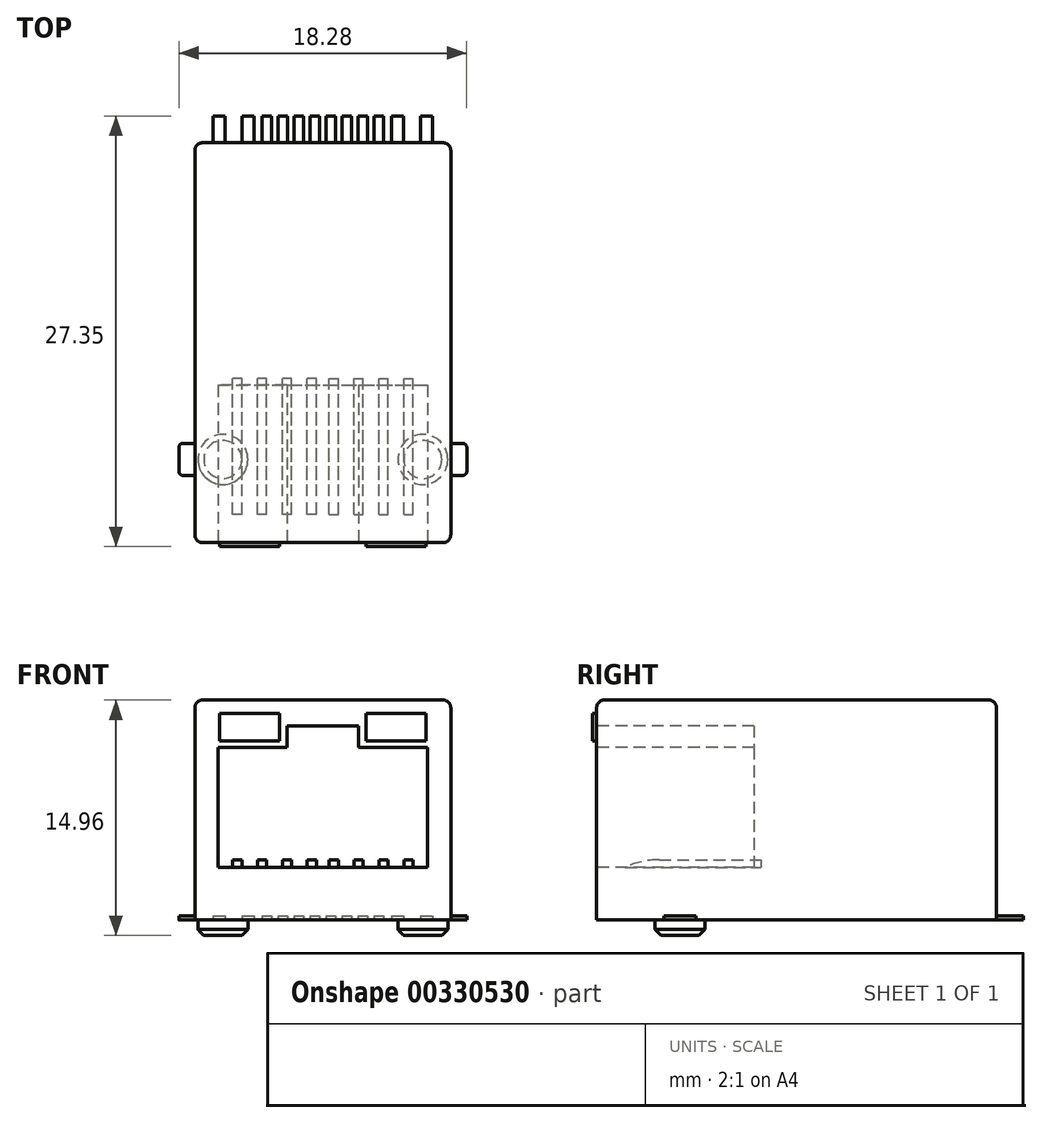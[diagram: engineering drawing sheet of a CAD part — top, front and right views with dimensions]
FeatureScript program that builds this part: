
annotation { "Feature Type Name" : "Feature", "Feature Type Description" : "" }
export const myFeature = defineFeature(function(context is Context, id is Id, definition is map)
    precondition{}
    {
        {
            var Q0;
            Q0=qCreatedBy(makeId("Top.planeOp"),FACE);
            var sketch = newSketch(context, id + "F0", { "sketchPlane" : qUnion([Q0])});
            skLineSegment(sketch, "E0.bottom", {"start": v(8.13, -12.7) * mm, "end": v(-8.13, -12.7) * mm});
            skLineSegment(sketch, "E0.top", {"start": v(8.13, 12.7) * mm, "end": v(-8.13, 12.7) * mm});
            skLineSegment(sketch, "E0.left", {"start": v(8.13, -12.7) * mm, "end": v(8.13, 12.7) * mm});
            skLineSegment(sketch, "E0.right", {"start": v(-8.13, -12.7) * mm, "end": v(-8.13, 12.7) * mm});
            skPoint(sketch, "E0.middle", {"position": v(0, 0) * mm});
            skSolve(sketch);
        }
        {
            var Q0;
            Q0=qSketchRegion(id+"F0",true);
            extrude(context, id + "F1", {"entities" : qUnion([Q0]), "depth" : 13.97 * mm, "offsetDistance" : 25 * mm});
        }
        {
            var Q0;
            Q0=makeQuery(id+"FJxkkNZS4rezTmz_1.boolean.opBoolean","MERGE",EDGE,{"derivedFrom":[makeQuery(id+"F1.opExtrude","SWEPT_EDGE",EDGE,{"disambiguationData":[OSD([sQuery(id+"F0.wireOp",EDGE,"E0.bottom"),sQuery(id+"F0.wireOp",EDGE,"E0.right")])]}),makeQuery(id+"FJxkkNZS4rezTmz_1.opExtrude","SWEPT_EDGE",EDGE,{"disambiguationData":[OSD([sQuery(id+"F9NPPUefej9rEKj_1.wireOp",EDGE,"desPq1yY-o5Qy-SBm8-Lvxq-VWqHqrpmvovc.bottom"),sQuery(id+"F9NPPUefej9rEKj_1.wireOp",EDGE,"desPq1yY-o5Qy-SBm8-Lvxq-VWqHqrpmvovc.right")])]})]});
            var Q1;
            Q1=makeQuery(id+"FJxkkNZS4rezTmz_1.boolean.opBoolean","MERGE",EDGE,{"derivedFrom":[makeQuery(id+"F1.opExtrude","SWEPT_EDGE",EDGE,{"disambiguationData":[OSD([sQuery(id+"F0.wireOp",EDGE,"E0.bottom"),sQuery(id+"F0.wireOp",EDGE,"E0.left")])]}),makeQuery(id+"FJxkkNZS4rezTmz_1.opExtrude","SWEPT_EDGE",EDGE,{"disambiguationData":[OSD([sQuery(id+"F9NPPUefej9rEKj_1.wireOp",EDGE,"desPq1yY-o5Qy-SBm8-Lvxq-VWqHqrpmvovc.bottom"),sQuery(id+"F9NPPUefej9rEKj_1.wireOp",EDGE,"desPq1yY-o5Qy-SBm8-Lvxq-VWqHqrpmvovc.left")])]})]});
            var Q2;
            Q2=makeQuery(id+"F1.opExtrude","SWEPT_EDGE",EDGE,{"disambiguationData":[OSD([sQuery(id+"F0.wireOp",EDGE,"E0.top"),sQuery(id+"F0.wireOp",EDGE,"E0.left")])]});
            var Q3;
            Q3=makeQuery(id+"F1.opExtrude","SWEPT_EDGE",EDGE,{"disambiguationData":[OSD([sQuery(id+"F0.wireOp",EDGE,"E0.top"),sQuery(id+"F0.wireOp",EDGE,"E0.right")])]});
            var Q4;
            Q4=makeQuery(id+"F1.opExtrude","CAP_EDGE",EDGE,{"disambiguationData":[OSD([sQuery(id+"F0.wireOp",EDGE,"E0.bottom")])],"isStart":false});
            var Q5;
            Q5=makeQuery(id+"F1.opExtrude","CAP_EDGE",EDGE,{"disambiguationData":[OSD([sQuery(id+"F0.wireOp",EDGE,"E0.right")])],"isStart":false});
            var Q6;
            Q6=makeQuery(id+"F1.opExtrude","CAP_EDGE",EDGE,{"disambiguationData":[OSD([sQuery(id+"F0.wireOp",EDGE,"E0.top")])],"isStart":false});
            var Q7;
            Q7=makeQuery(id+"F1.opExtrude","CAP_EDGE",EDGE,{"disambiguationData":[OSD([sQuery(id+"F0.wireOp",EDGE,"E0.left")])],"isStart":false});
            var Q8;
            Q8=makeQuery(id+"FJxkkNZS4rezTmz_1.opExtrude","CAP_EDGE",EDGE,{"disambiguationData":[OSD([sQuery(id+"F9NPPUefej9rEKj_1.wireOp",EDGE,"desPq1yY-o5Qy-SBm8-Lvxq-VWqHqrpmvovc.bottom")])],"isStart":false});
            var Q9;
            Q9=makeQuery(id+"FJxkkNZS4rezTmz_1.opExtrude","CAP_EDGE",EDGE,{"disambiguationData":[OSD([sQuery(id+"F9NPPUefej9rEKj_1.wireOp",EDGE,"desPq1yY-o5Qy-SBm8-Lvxq-VWqHqrpmvovc.right")])],"isStart":false});
            var Q10;
            Q10=makeQuery(id+"FJxkkNZS4rezTmz_1.opExtrude","CAP_EDGE",EDGE,{"disambiguationData":[OSD([sQuery(id+"F9NPPUefej9rEKj_1.wireOp",EDGE,"desPq1yY-o5Qy-SBm8-Lvxq-VWqHqrpmvovc.left")])],"isStart":false});
            fillet(context, id + "F2", {"entities" : qUnion([Q0, Q1, Q2, Q3, Q4, Q5, Q6, Q7, Q8, Q9, Q10]), "radius" : .5 * mm, "tangentPropagation" : true, "allowEdgeOverflow" : false});
        }
        {
            var Q0;
            Q0=makeQuery(id+"FJxkkNZS4rezTmz_1.boolean.opBoolean","MERGE",FACE,{"derivedFrom":[makeQuery(id+"F1.opExtrude","SWEPT_FACE",FACE,{"disambiguationData":[OSD([sQuery(id+"F0.wireOp",EDGE,"E0.bottom")])]}),makeQuery(id+"FJxkkNZS4rezTmz_1.opExtrude","SWEPT_FACE",FACE,{"disambiguationData":[OSD([sQuery(id+"F9NPPUefej9rEKj_1.wireOp",EDGE,"desPq1yY-o5Qy-SBm8-Lvxq-VWqHqrpmvovc.bottom")])]})]});
            var sketch = newSketch(context, id + "F3", { "sketchPlane" : qUnion([Q0])});
            skLineSegment(sketch, "E1", {"start": v(0, 13.47) * mm, "end": v(0, 0) * mm, "construction": true});
            skLineSegment(sketch, "E2", {"start": v(0, 12.33) * mm, "end": v(2.28, 12.33) * mm});
            skLineSegment(sketch, "E3", {"start": v(2.28, 12.33) * mm, "end": v(2.28, 10.96) * mm});
            skLineSegment(sketch, "E4", {"start": v(2.28, 10.96) * mm, "end": v(6.66, 10.96) * mm});
            skLineSegment(sketch, "E5", {"start": v(6.66, 10.96) * mm, "end": v(6.66, 3.33) * mm});
            skLineSegment(sketch, "E6", {"start": v(6.66, 3.33) * mm, "end": v(0, 3.33) * mm});
            skLineSegment(sketch, "E7.MirrorCS", {"start": v(-6.66, 3.33) * mm, "end": v(0, 3.33) * mm});
            skLineSegment(sketch, "E8.MirrorCS", {"start": v(-6.66, 10.96) * mm, "end": v(-6.66, 3.33) * mm});
            skLineSegment(sketch, "E9.MirrorCS", {"start": v(-2.28, 10.96) * mm, "end": v(-6.66, 10.96) * mm});
            skLineSegment(sketch, "E10.MirrorCS", {"start": v(0, 12.33) * mm, "end": v(-2.28, 12.33) * mm});
            skLineSegment(sketch, "E11.MirrorCS", {"start": v(-2.28, 12.33) * mm, "end": v(-2.28, 10.96) * mm});
            skSolve(sketch);
        }
        {
            var Q0;
            Q0=qSketchRegion(id+"F3",true);
            extrude(context, id + "F4", {"entities" : qUnion([Q0]), "operationType" : NewBodyOperationType.REMOVE, "oppositeDirection" : true, "depth" : 10 * mm, "offsetDistance" : 25 * mm});
        }
        {
            var Q0;
            Q0=makeQuery(id+"F4.boolean.opBoolean","COPY",FACE,{"derivedFrom":makeQuery(id+"F4.opExtrude","SWEPT_FACE",FACE,{"disambiguationData":[OSD([sQuery(id+"F3.wireOp",EDGE,"E6"),sQuery(id+"F3.wireOp",EDGE,"E7.MirrorCS")])]})});
            var sketch = newSketch(context, id + "F5", { "sketchPlane" : qUnion([Q0])});
            skLineSegment(sketch, "E12", {"start": v(0, -12.7) * mm, "end": v(0, -2.7) * mm, "construction": true});
            skLineSegment(sketch, "E13.bottom", {"start": v(0.4, -10.9) * mm, "end": v(0.99, -10.9) * mm});
            skLineSegment(sketch, "E13.top", {"start": v(0.4, -2.26) * mm, "end": v(0.99, -2.26) * mm});
            skLineSegment(sketch, "E13.left", {"start": v(0.4, -10.9) * mm, "end": v(0.4, -2.26) * mm});
            skLineSegment(sketch, "E13.right", {"start": v(0.99, -10.9) * mm, "end": v(0.99, -2.26) * mm});
            skLineSegment(sketch, "E14.1.0.0", {"start": v(1.98, -10.9) * mm, "end": v(2.57, -10.9) * mm});
            skLineSegment(sketch, "E14.1.0.1", {"start": v(1.98, -2.26) * mm, "end": v(2.57, -2.26) * mm});
            skLineSegment(sketch, "E14.1.0.2", {"start": v(1.98, -10.9) * mm, "end": v(1.98, -2.26) * mm});
            skLineSegment(sketch, "E14.1.0.3", {"start": v(2.57, -10.9) * mm, "end": v(2.57, -2.26) * mm});
            skLineSegment(sketch, "E14.2.0.0", {"start": v(3.56, -10.9) * mm, "end": v(4.15, -10.9) * mm});
            skLineSegment(sketch, "E14.2.0.1", {"start": v(3.56, -2.26) * mm, "end": v(4.15, -2.26) * mm});
            skLineSegment(sketch, "E14.2.0.2", {"start": v(3.56, -10.9) * mm, "end": v(3.56, -2.26) * mm});
            skLineSegment(sketch, "E14.2.0.3", {"start": v(4.15, -10.9) * mm, "end": v(4.15, -2.26) * mm});
            skLineSegment(sketch, "E14.3.0.0", {"start": v(5.14, -10.9) * mm, "end": v(5.73, -10.9) * mm});
            skLineSegment(sketch, "E14.3.0.1", {"start": v(5.14, -2.26) * mm, "end": v(5.73, -2.26) * mm});
            skLineSegment(sketch, "E14.3.0.2", {"start": v(5.14, -10.9) * mm, "end": v(5.14, -2.26) * mm});
            skLineSegment(sketch, "E14.3.0.3", {"start": v(5.73, -10.9) * mm, "end": v(5.73, -2.26) * mm});
            skLineSegment(sketch, "E14.direction1", {"start": v(0.4, -10.9) * mm, "end": v(1.98, -10.9) * mm, "construction": true});
            skLineSegment(sketch, "E15.MirrorCS", {"start": v(-0.4, -10.9) * mm, "end": v(-0.99, -10.9) * mm});
            skLineSegment(sketch, "E16.MirrorCS", {"start": v(-4.15, -10.9) * mm, "end": v(-4.15, -2.26) * mm});
            skLineSegment(sketch, "E17.MirrorCS", {"start": v(-3.56, -10.9) * mm, "end": v(-3.56, -2.26) * mm});
            skLineSegment(sketch, "E18.MirrorCS", {"start": v(-3.56, -2.26) * mm, "end": v(-4.15, -2.26) * mm});
            skLineSegment(sketch, "E19.MirrorCS", {"start": v(-3.56, -10.9) * mm, "end": v(-4.15, -10.9) * mm});
            skLineSegment(sketch, "E20.MirrorCS", {"start": v(-2.57, -10.9) * mm, "end": v(-2.57, -2.26) * mm});
            skLineSegment(sketch, "E21.MirrorCS", {"start": v(-1.98, -10.9) * mm, "end": v(-1.98, -2.26) * mm});
            skLineSegment(sketch, "E22.MirrorCS", {"start": v(-1.98, -2.26) * mm, "end": v(-2.57, -2.26) * mm});
            skLineSegment(sketch, "E23.MirrorCS", {"start": v(-1.98, -10.9) * mm, "end": v(-2.57, -10.9) * mm});
            skLineSegment(sketch, "E24.MirrorCS", {"start": v(-0.99, -10.9) * mm, "end": v(-0.99, -2.26) * mm});
            skLineSegment(sketch, "E25.MirrorCS", {"start": v(-0.4, -10.9) * mm, "end": v(-0.4, -2.26) * mm});
            skLineSegment(sketch, "E26.MirrorCS", {"start": v(-0.4, -2.26) * mm, "end": v(-0.99, -2.26) * mm});
            skLineSegment(sketch, "E27.MirrorCS", {"start": v(-5.73, -10.9) * mm, "end": v(-5.73, -2.26) * mm});
            skLineSegment(sketch, "E28.MirrorCS", {"start": v(-5.14, -10.9) * mm, "end": v(-5.14, -2.26) * mm});
            skLineSegment(sketch, "E29.MirrorCS", {"start": v(-5.14, -2.26) * mm, "end": v(-5.73, -2.26) * mm});
            skLineSegment(sketch, "E30.MirrorCS", {"start": v(-0.4, -10.9) * mm, "end": v(-1.98, -10.9) * mm, "construction": true});
            skLineSegment(sketch, "E31.MirrorCS", {"start": v(-5.14, -10.9) * mm, "end": v(-5.73, -10.9) * mm});
            skSolve(sketch);
        }
        {
            var Q0;
            Q0=qSketchRegion(id+"F5",true);
            extrude(context, id + "F6", {"entities" : qUnion([Q0]), "depth" : .5 * mm, "offsetDistance" : 25 * mm});
        }
        {
            var Q0;
            Q0=makeQuery(id+"F6.opExtrude","CAP_EDGE",EDGE,{"disambiguationData":[OSD([sQuery(id+"F5.wireOp",EDGE,"E31.MirrorCS")])],"isStart":false});
            var Q1;
            Q1=makeQuery(id+"F6.opExtrude","CAP_EDGE",EDGE,{"disambiguationData":[OSD([sQuery(id+"F5.wireOp",EDGE,"E19.MirrorCS")])],"isStart":false});
            var Q2;
            Q2=makeQuery(id+"F6.opExtrude","CAP_EDGE",EDGE,{"disambiguationData":[OSD([sQuery(id+"F5.wireOp",EDGE,"E23.MirrorCS")])],"isStart":false});
            var Q3;
            Q3=makeQuery(id+"F6.opExtrude","CAP_EDGE",EDGE,{"disambiguationData":[OSD([sQuery(id+"F5.wireOp",EDGE,"E15.MirrorCS")])],"isStart":false});
            var Q4;
            Q4=makeQuery(id+"F6.opExtrude","CAP_EDGE",EDGE,{"disambiguationData":[OSD([sQuery(id+"F5.wireOp",EDGE,"E13.bottom")])],"isStart":false});
            var Q5;
            Q5=makeQuery(id+"F6.opExtrude","CAP_EDGE",EDGE,{"disambiguationData":[OSD([sQuery(id+"F5.wireOp",EDGE,"E14.1.0.0")])],"isStart":false});
            var Q6;
            Q6=makeQuery(id+"F6.opExtrude","CAP_EDGE",EDGE,{"disambiguationData":[OSD([sQuery(id+"F5.wireOp",EDGE,"E14.2.0.0")])],"isStart":false});
            var Q7;
            Q7=makeQuery(id+"F6.opExtrude","CAP_EDGE",EDGE,{"disambiguationData":[OSD([sQuery(id+"F5.wireOp",EDGE,"E14.3.0.0")])],"isStart":false});
            fillet(context, id + "F7", {"entities" : qUnion([Q0, Q1, Q2, Q3, Q4, Q5, Q6, Q7]), "radius" : 5 * mm, "tangentPropagation" : true, "allowEdgeOverflow" : false});
        }
        {
            var Q0;
            Q0=makeQuery(id+"F1.opExtrude","CAP_FACE",FACE,{"disambiguationData":[OSD([sQuery(id+"F0.wireOp",EDGE,"E0.bottom"),sQuery(id+"F0.wireOp",EDGE,"E0.top"),sQuery(id+"F0.wireOp",EDGE,"E0.left"),sQuery(id+"F0.wireOp",EDGE,"E0.right")])],"isStart":true});
            var sketch = newSketch(context, id + "F8", { "sketchPlane" : qUnion([Q0])});
            skCircle(sketch, "E32", {"center": v(6.35, 7.42) * mm, "radius": 1.59 * mm});
            skLineSegment(sketch, "E33", {"start": v(0, 12.7) * mm, "end": v(0, -12.7) * mm, "construction": true});
            skCircle(sketch, "E34.MirrorC", {"center": v(-6.35, 7.42) * mm, "radius": 1.59 * mm});
            skSolve(sketch);
        }
        {
            var Q0;
            Q0 = qSketchRegion(id + "F8", true);
            extrude(context, id + "F9", {"entities" : qUnion([Q0]), "operationType" : NewBodyOperationType.ADD, "depth" : 1 * mm, "offsetDistance" : 25.4 * mm});
        }
        {
            var Q0;
            Q0=makeQuery(id+"F1.opExtrude","CAP_FACE",FACE,{"disambiguationData":[OSD([sQuery(id+"F0.wireOp",EDGE,"E0.bottom"),sQuery(id+"F0.wireOp",EDGE,"E0.top"),sQuery(id+"F0.wireOp",EDGE,"E0.left"),sQuery(id+"F0.wireOp",EDGE,"E0.right")])],"isStart":true});
            var sketch = newSketch(context, id + "F10", { "sketchPlane" : qUnion([Q0])});
            skLineSegment(sketch, "E35", {"start": v(0, -12.7) * mm, "end": v(0, 12.7) * mm, "construction": true});
            skLineSegment(sketch, "E36.bottom", {"start": v(0.2, -12.62) * mm, "end": v(0.81, -12.62) * mm});
            skLineSegment(sketch, "E36.top", {"start": v(0.2, -14.4) * mm, "end": v(0.81, -14.4) * mm});
            skLineSegment(sketch, "E36.left", {"start": v(0.2, -12.62) * mm, "end": v(0.2, -14.4) * mm});
            skLineSegment(sketch, "E36.right", {"start": v(0.81, -12.62) * mm, "end": v(0.81, -14.4) * mm});
            skPoint(sketch, "E36.middle", {"position": v(0.5, -13.51) * mm});
            skLineSegment(sketch, "E37.1.0.0", {"start": v(1.83, -12.62) * mm, "end": v(1.83, -14.4) * mm});
            skLineSegment(sketch, "E37.1.0.1", {"start": v(1.22, -14.4) * mm, "end": v(1.83, -14.4) * mm});
            skLineSegment(sketch, "E37.1.0.2", {"start": v(1.22, -12.62) * mm, "end": v(1.22, -14.4) * mm});
            skPoint(sketch, "E37.1.0.3", {"position": v(1.52, -13.51) * mm});
            skLineSegment(sketch, "E37.1.0.4", {"start": v(1.22, -12.62) * mm, "end": v(1.83, -12.62) * mm});
            skLineSegment(sketch, "E37.2.0.0", {"start": v(2.84, -12.62) * mm, "end": v(2.84, -14.4) * mm});
            skLineSegment(sketch, "E37.2.0.1", {"start": v(2.24, -14.4) * mm, "end": v(2.84, -14.4) * mm});
            skLineSegment(sketch, "E37.2.0.2", {"start": v(2.24, -12.62) * mm, "end": v(2.24, -14.4) * mm});
            skPoint(sketch, "E37.2.0.3", {"position": v(2.54, -13.51) * mm});
            skLineSegment(sketch, "E37.2.0.4", {"start": v(2.24, -12.62) * mm, "end": v(2.84, -12.62) * mm});
            skLineSegment(sketch, "E37.3.0.0", {"start": v(3.86, -12.62) * mm, "end": v(3.86, -14.4) * mm});
            skLineSegment(sketch, "E37.3.0.1", {"start": v(3.25, -14.4) * mm, "end": v(3.86, -14.4) * mm});
            skLineSegment(sketch, "E37.3.0.2", {"start": v(3.25, -12.62) * mm, "end": v(3.25, -14.4) * mm});
            skPoint(sketch, "E37.3.0.3", {"position": v(3.56, -13.51) * mm});
            skLineSegment(sketch, "E37.3.0.4", {"start": v(3.25, -12.62) * mm, "end": v(3.86, -12.62) * mm});
            skLineSegment(sketch, "E37.direction1", {"start": v(0.2, -14.4) * mm, "end": v(1.22, -14.4) * mm, "construction": true});
            skLineSegment(sketch, "E38.bottom", {"start": v(4.37, -12.62) * mm, "end": v(5.13, -12.62) * mm});
            skLineSegment(sketch, "E38.top", {"start": v(4.37, -14.4) * mm, "end": v(5.13, -14.4) * mm});
            skLineSegment(sketch, "E38.left", {"start": v(4.37, -12.62) * mm, "end": v(4.37, -14.4) * mm});
            skLineSegment(sketch, "E38.right", {"start": v(5.13, -12.62) * mm, "end": v(5.13, -14.4) * mm});
            skPoint(sketch, "E38.middle", {"position": v(4.75, -13.51) * mm});
            skPoint(sketch, "E39.1.0.0", {"position": v(6.58, -13.51) * mm});
            skLineSegment(sketch, "E39.1.0.1", {"start": v(6.96, -12.62) * mm, "end": v(6.96, -14.4) * mm});
            skLineSegment(sketch, "E39.1.0.2", {"start": v(6.2, -12.62) * mm, "end": v(6.2, -14.4) * mm});
            skLineSegment(sketch, "E39.1.0.3", {"start": v(6.2, -12.62) * mm, "end": v(6.96, -12.62) * mm});
            skLineSegment(sketch, "E39.1.0.4", {"start": v(6.2, -14.4) * mm, "end": v(6.96, -14.4) * mm});
            skLineSegment(sketch, "E39.direction1", {"start": v(4.37, -14.4) * mm, "end": v(6.2, -14.4) * mm, "construction": true});
            skLineSegment(sketch, "E40.MirrorCS", {"start": v(-0.2, -14.4) * mm, "end": v(-0.81, -14.4) * mm});
            skLineSegment(sketch, "E41.MirrorCS", {"start": v(-2.24, -12.62) * mm, "end": v(-2.84, -12.62) * mm});
            skLineSegment(sketch, "E42.MirrorCS", {"start": v(-1.22, -12.62) * mm, "end": v(-1.83, -12.62) * mm});
            skLineSegment(sketch, "E43.MirrorCS", {"start": v(-1.22, -14.4) * mm, "end": v(-1.83, -14.4) * mm});
            skLineSegment(sketch, "E44.MirrorCS", {"start": v(-3.25, -14.4) * mm, "end": v(-3.86, -14.4) * mm});
            skLineSegment(sketch, "E45.MirrorCS", {"start": v(-3.25, -12.62) * mm, "end": v(-3.86, -12.62) * mm});
            skLineSegment(sketch, "E46.MirrorCS", {"start": v(-0.2, -14.4) * mm, "end": v(-1.22, -14.4) * mm, "construction": true});
            skLineSegment(sketch, "E47.MirrorCS", {"start": v(-0.2, -12.62) * mm, "end": v(-0.81, -12.62) * mm});
            skLineSegment(sketch, "E48.MirrorCS", {"start": v(-2.24, -14.4) * mm, "end": v(-2.84, -14.4) * mm});
            skLineSegment(sketch, "E49.MirrorCS", {"start": v(-4.37, -14.4) * mm, "end": v(-5.13, -14.4) * mm});
            skLineSegment(sketch, "E50.MirrorCS", {"start": v(-2.84, -12.62) * mm, "end": v(-2.84, -14.4) * mm});
            skLineSegment(sketch, "E51.MirrorCS", {"start": v(-1.22, -12.62) * mm, "end": v(-1.22, -14.4) * mm});
            skLineSegment(sketch, "E52.MirrorCS", {"start": v(-3.86, -12.62) * mm, "end": v(-3.86, -14.4) * mm});
            skLineSegment(sketch, "E53.MirrorCS", {"start": v(-6.2, -12.62) * mm, "end": v(-6.2, -14.4) * mm});
            skPoint(sketch, "E54.MirrorP", {"position": v(-2.54, -13.51) * mm});
            skLineSegment(sketch, "E55.MirrorCS", {"start": v(-2.24, -12.62) * mm, "end": v(-2.24, -14.4) * mm});
            skPoint(sketch, "E56.MirrorP", {"position": v(-6.58, -13.51) * mm});
            skPoint(sketch, "E57.MirrorP", {"position": v(-0.5, -13.51) * mm});
            skLineSegment(sketch, "E58.MirrorCS", {"start": v(-6.2, -12.62) * mm, "end": v(-6.96, -12.62) * mm});
            skPoint(sketch, "E59.MirrorP", {"position": v(-3.56, -13.51) * mm});
            skLineSegment(sketch, "E60.MirrorCS", {"start": v(-4.37, -12.62) * mm, "end": v(-5.13, -12.62) * mm});
            skLineSegment(sketch, "E61.MirrorCS", {"start": v(-4.37, -14.4) * mm, "end": v(-6.2, -14.4) * mm, "construction": true});
            skPoint(sketch, "E62.MirrorP", {"position": v(-4.75, -13.51) * mm});
            skLineSegment(sketch, "E63.MirrorCS", {"start": v(-5.13, -12.62) * mm, "end": v(-5.13, -14.4) * mm});
            skPoint(sketch, "E64.MirrorP", {"position": v(-1.52, -13.51) * mm});
            skLineSegment(sketch, "E65.MirrorCS", {"start": v(-3.25, -12.62) * mm, "end": v(-3.25, -14.4) * mm});
            skLineSegment(sketch, "E66.MirrorCS", {"start": v(-6.2, -14.4) * mm, "end": v(-6.96, -14.4) * mm});
            skLineSegment(sketch, "E67.MirrorCS", {"start": v(-0.2, -12.62) * mm, "end": v(-0.2, -14.4) * mm});
            skLineSegment(sketch, "E68.MirrorCS", {"start": v(-6.96, -12.62) * mm, "end": v(-6.96, -14.4) * mm});
            skLineSegment(sketch, "E69.MirrorCS", {"start": v(-1.83, -12.62) * mm, "end": v(-1.83, -14.4) * mm});
            skLineSegment(sketch, "E70.MirrorCS", {"start": v(-0.81, -12.62) * mm, "end": v(-0.81, -14.4) * mm});
            skLineSegment(sketch, "E71.MirrorCS", {"start": v(-4.37, -12.62) * mm, "end": v(-4.37, -14.4) * mm});
            skLineSegment(sketch, "E72.bottom", {"start": v(8.13, 8.43) * mm, "end": v(8.9, 8.43) * mm});
            skLineSegment(sketch, "E72.top", {"start": v(8.13, 6.4) * mm, "end": v(8.9, 6.4) * mm});
            skLineSegment(sketch, "E72.left", {"start": v(8.13, 8.43) * mm, "end": v(8.13, 6.4) * mm});
            skLineSegment(sketch, "E72.right", {"start": v(9.14, 8.18) * mm, "end": v(9.14, 6.65) * mm});
            skPoint(sketch, "E72.middle", {"position": v(8.64, 7.42) * mm});
            skPoint(sketch, "E73.visualSharp", {"position": v(9.14, 6.4) * mm});
            skArc(sketch, "E73.filletArc", {"start": v(8.9, 6.4) * mm, "mid": v(9.07, 6.48) * mm, "end": v(9.14, 6.65) * mm});
            skPoint(sketch, "E74.visualSharp", {"position": v(9.14, 8.43) * mm});
            skArc(sketch, "E74.filletArc", {"start": v(9.14, 8.18) * mm, "mid": v(9.07, 8.36) * mm, "end": v(8.9, 8.43) * mm});
            skArc(sketch, "E75.MirrorCS", {"start": v(-9.14, 8.18) * mm, "mid": v(-9.07, 8.36) * mm, "end": v(-8.9, 8.43) * mm});
            skArc(sketch, "E76.MirrorCS", {"start": v(-8.9, 6.4) * mm, "mid": v(-9.07, 6.48) * mm, "end": v(-9.14, 6.65) * mm});
            skLineSegment(sketch, "E77.MirrorCS", {"start": v(-9.14, 8.18) * mm, "end": v(-9.14, 6.65) * mm});
            skLineSegment(sketch, "E78.MirrorCS", {"start": v(-8.13, 8.43) * mm, "end": v(-8.13, 6.4) * mm});
            skLineSegment(sketch, "E79.MirrorCS", {"start": v(-8.13, 8.43) * mm, "end": v(-8.9, 8.43) * mm});
            skPoint(sketch, "E80.MirrorP", {"position": v(-9.14, 8.43) * mm});
            skLineSegment(sketch, "E81.MirrorCS", {"start": v(-8.13, 6.4) * mm, "end": v(-8.9, 6.4) * mm});
            skPoint(sketch, "E82.MirrorP", {"position": v(-9.14, 6.4) * mm});
            skPoint(sketch, "E83.MirrorP", {"position": v(-8.64, 7.42) * mm});
            skSolve(sketch);
        }
        {
            var Q0;
            Q0 = qSketchRegion(id + "F10", true);
            extrude(context, id + "F11", {"entities" : qUnion([Q0]), "operationType" : NewBodyOperationType.ADD, "oppositeDirection" : true, "depth" : 0.25 * mm, "offsetDistance" : 25.4 * mm});
        }
        {
            var Q0;
            Q0=makeQuery(id+"F1.opExtrude","SWEPT_FACE",FACE,{"disambiguationData":[OSD([sQuery(id+"F0.wireOp",EDGE,"E0.bottom")])]});
            var sketch = newSketch(context, id + "F12", { "sketchPlane" : qUnion([Q0])});
            skLineSegment(sketch, "E84", {"start": v(0, 13.28) * mm, "end": v(0, 10.92) * mm, "construction": true});
            skPoint(sketch, "E84.startSnap0", {"position": v(0, 13.47) * mm});
            skLineSegment(sketch, "E85.bottom", {"start": v(-6.55, 13.11) * mm, "end": v(-2.74, 13.11) * mm});
            skLineSegment(sketch, "E85.top", {"start": v(-6.55, 11.37) * mm, "end": v(-2.74, 11.37) * mm});
            skLineSegment(sketch, "E85.left", {"start": v(-6.55, 13.11) * mm, "end": v(-6.55, 11.37) * mm});
            skLineSegment(sketch, "E85.right", {"start": v(-2.74, 13.11) * mm, "end": v(-2.74, 11.37) * mm});
            skLineSegment(sketch, "E86.MirrorCS", {"start": v(6.55, 13.11) * mm, "end": v(2.74, 13.11) * mm});
            skLineSegment(sketch, "E87.MirrorCS", {"start": v(2.74, 13.11) * mm, "end": v(2.74, 11.37) * mm});
            skLineSegment(sketch, "E88.MirrorCS", {"start": v(6.55, 13.11) * mm, "end": v(6.55, 11.37) * mm});
            skLineSegment(sketch, "E89.MirrorCS", {"start": v(6.55, 11.37) * mm, "end": v(2.74, 11.37) * mm});
            skSolve(sketch);
        }
        {
            var Q0;
            Q0 = qSketchRegion(id + "F12", true);
            extrude(context, id + "F13", {"entities" : qUnion([Q0]), "depth" : 0.25 * mm, "offsetDistance" : 25.4 * mm});
        }
        {
            var Q0;
            Q0=makeQuery(id+"F9.opExtrude","CAP_EDGE",EDGE,{"disambiguationData":[OSD([sQuery(id+"F8.wireOp",EDGE,"E32")])],"isStart":false});
            var Q1;
            Q1=makeQuery(id+"F9.opExtrude","CAP_EDGE",EDGE,{"disambiguationData":[OSD([sQuery(id+"F8.wireOp",EDGE,"E34.MirrorC")])],"isStart":false});
            chamfer(context, id + "F14", {"entities" : qUnion([Q0, Q1]), "width" : 0.38 * mm, "tangentPropagation" : true});
        }
    });
